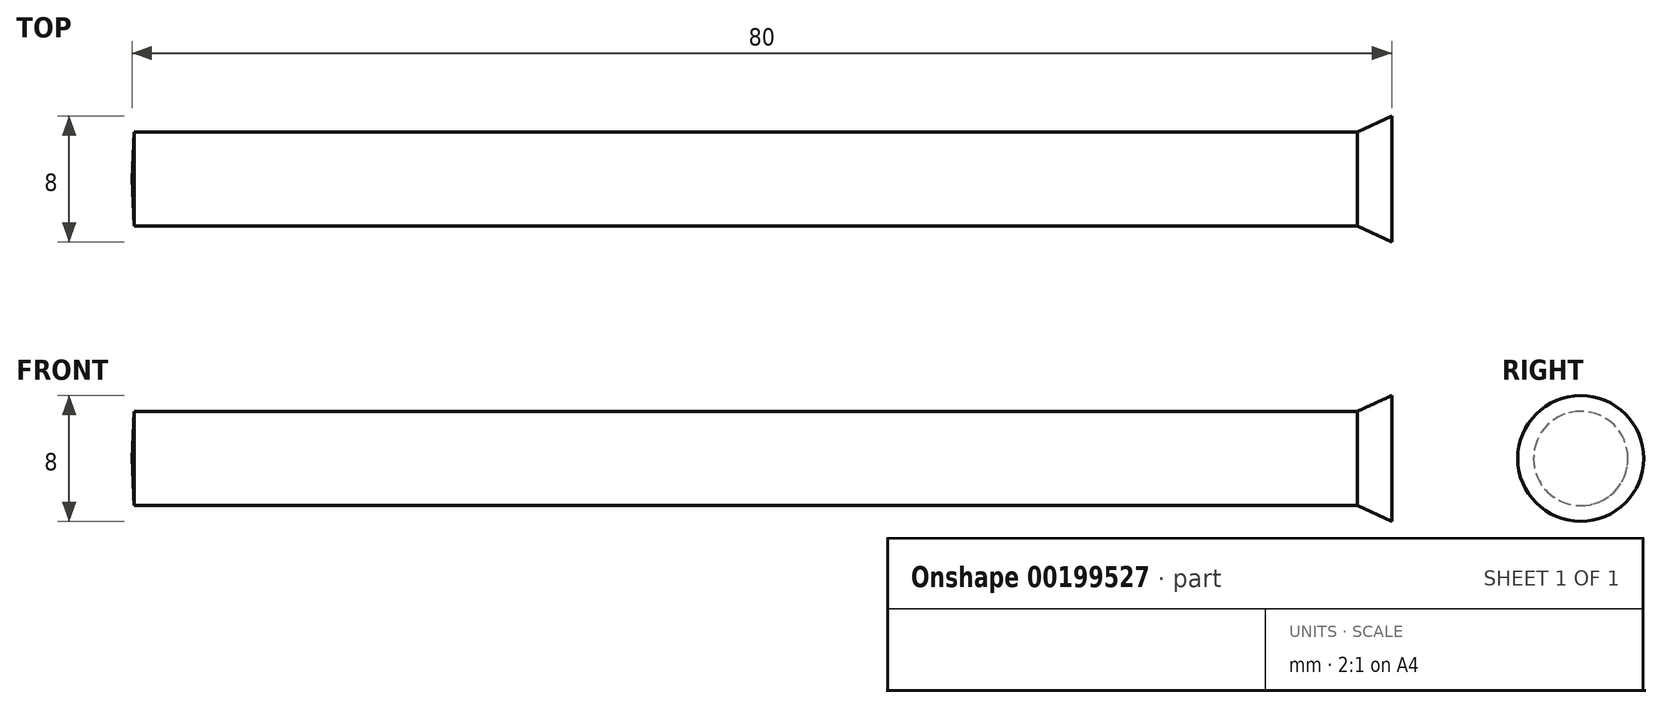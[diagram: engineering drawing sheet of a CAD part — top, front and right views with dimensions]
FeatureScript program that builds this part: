
annotation { "Feature Type Name" : "Feature", "Feature Type Description" : "" }
export const myFeature = defineFeature(function(context is Context, id is Id, definition is map)
    precondition{}
    {
        {
            var Q0;
            Q0=qCreatedBy(makeId("Front.planeOp"),FACE);
            var sketch = newSketch(context, id + "F0", { "sketchPlane" : qUnion([Q0])});
            skLineSegment(sketch, "E0", {"start": v(-48.04, 0) * mm, "end": v(31.96, 0) * mm});
            skLineSegment(sketch, "E1", {"start": v(31.96, 0) * mm, "end": v(31.96, -4) * mm});
            skLineSegment(sketch, "E2", {"start": v(31.96, -4) * mm, "end": v(29.78, -3) * mm});
            skLineSegment(sketch, "E3", {"start": v(29.78, -3) * mm, "end": v(-47.92, -3) * mm});
            skLineSegment(sketch, "E4", {"start": v(-47.92, -3) * mm, "end": v(-48.04, 0) * mm});
            skSolve(sketch);
        }
        {
            var Q0;
            Q0=makeQuery(id+"F0.imprint","IMPRINT",FACE,{"disambiguationData":[TD([[makeQuery(id+"F0.imprint","IMPRINT",EDGE,{"derivedFrom":sQuery(id+"F0.wireOp",EDGE,"E0")}),-1.0]])]});
            var Q1;
            Q1=sQuery(id+"F0.wireOp",EDGE,"E0");
            revolve(context, id + "F1", {"entities" : qUnion([Q0]), "axis" : qUnion([Q1]), "revolveType" : RevolveType.FULL});
        }
    });
